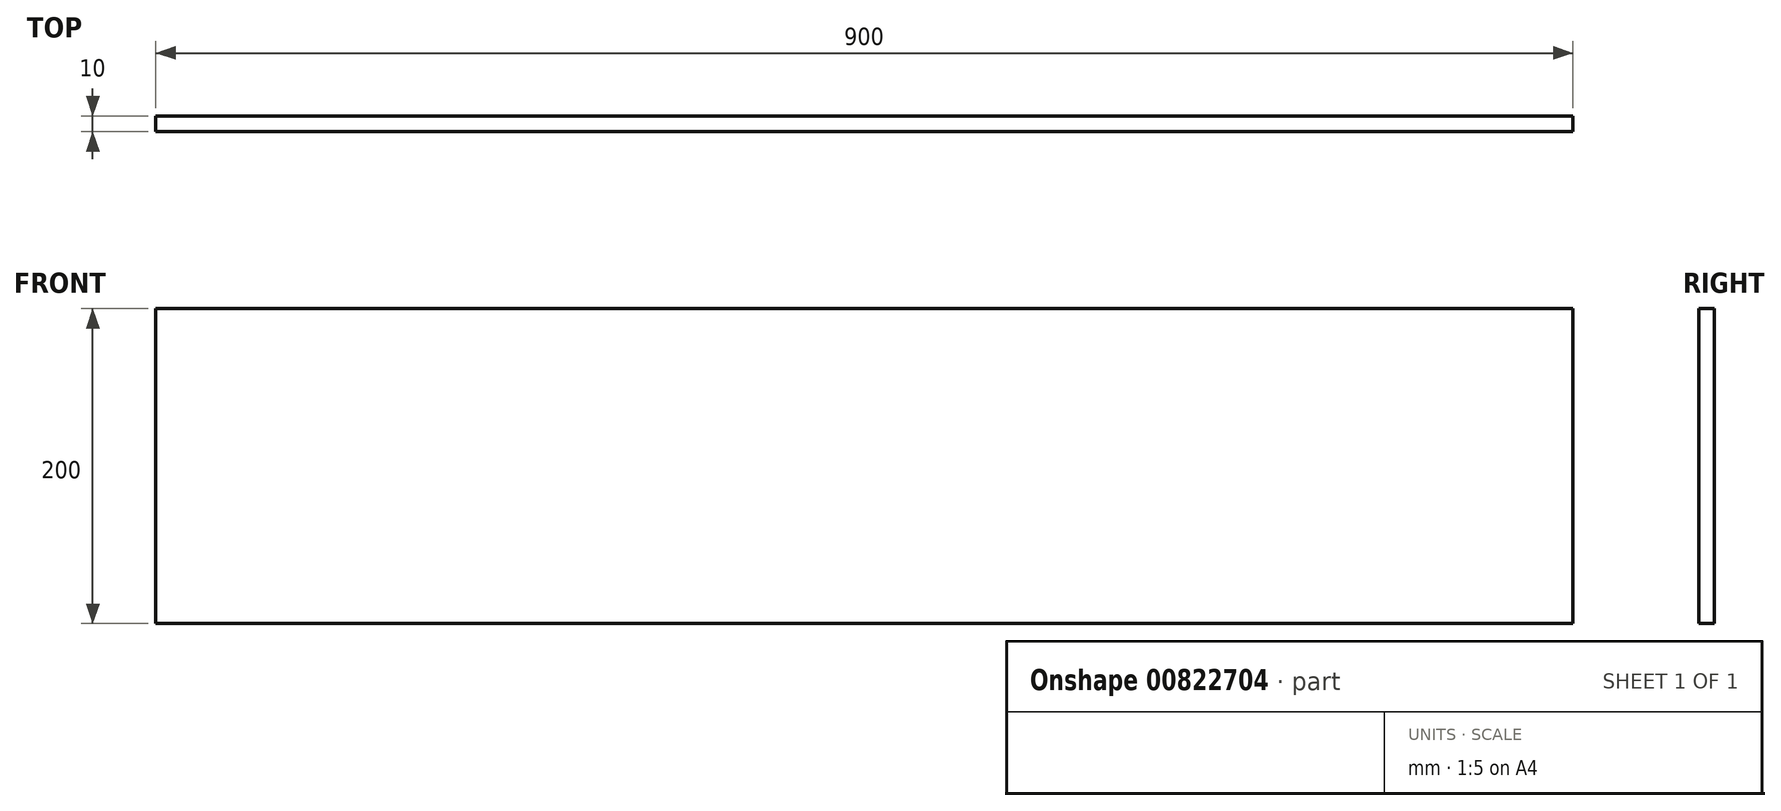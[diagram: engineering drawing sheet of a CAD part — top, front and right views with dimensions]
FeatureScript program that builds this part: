
annotation { "Feature Type Name" : "Feature", "Feature Type Description" : "" }
export const myFeature = defineFeature(function(context is Context, id is Id, definition is map)
    precondition{}
    {
        {
            var Q0;
            Q0=qCreatedBy(makeId("Front.planeOp"),FACE);
            var sketch = newSketch(context, id + "F0", { "sketchPlane" : qUnion([Q0])});
            skLineSegment(sketch, "E0.bottom", {"start": v(0, 0) * mm, "end": v(900, 0) * mm});
            skLineSegment(sketch, "E0.top", {"start": v(0, 200) * mm, "end": v(900, 200) * mm});
            skLineSegment(sketch, "E0.left", {"start": v(0, 0) * mm, "end": v(0, 200) * mm});
            skLineSegment(sketch, "E0.right", {"start": v(900, 0) * mm, "end": v(900, 200) * mm});
            skSolve(sketch);
        }
        {
            var Q0;
            Q0 = qSketchRegion(id + "F0", true);
            extrude(context, id + "F1", {"entities" : qUnion([Q0]), "depth" : 10 * mm, "offsetDistance" : 25 * mm});
        }
    });
